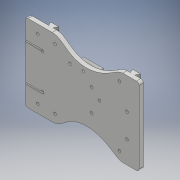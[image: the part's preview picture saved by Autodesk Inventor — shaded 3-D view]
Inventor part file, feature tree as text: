
AUTODESK INVENTOR PART (.ipt)
format: ipt  version: 2017 (Build 210142000, 142)  size: 294,912 bytes
history: native  units: mm
features: sketch x9, extrude x6, hole x3, chamfer x1, fillet x1
ambient origin geometry x8: Origin, YZ Plane, XZ Plane, XY Plane, X Axis, Y Axis, Z Axis, Center Point
bodies: Solid1 (feature_tree)
feature tree (20):
  extrude  "Extrusion1"  Depth=90.0mm
  sketch  "Sketch2"  dims[d2=20.0mm d3=41.0mm]
  extrude  "Extrusion7"  Depth=41.0mm
  extrude  "Extrusion3"  Depth=1.5mm
  extrude  "Extrusion4"  Depth=9.5mm
  extrude  "Extrusion5"  Depth=5.0mm
  hole  "Hole1"  [1 undecoded]
  hole  "Hole2"  [1 undecoded]
  chamfer  "Chamfer1"  Distance=36.0mm
  fillet  "Fillet1"  Radius=11.0mm
  hole  "Hole3"  [1 undecoded]
  extrude  "Extrusion8"  Depth=20.0mm
  sketch  "Sketch1"  dims[d0=132.0mm d1=90.0mm]
  sketch  "Sketch3"  dims[d4=1.5mm d5=1.5mm]
  sketch  "Sketch4"  dims[d6=5.0mm d7=0.0mm d8=9.5mm]
  sketch  "Sketch5"  dims[d10=22.0mm d11=5.0mm]
  sketch  "Sketch6"  dims[d15=4.5mm d23=120.0mm d24=0.0mm]
  sketch  "Sketch7"  dims[d25=3.0mm d26=70.0mm]
  sketch  "Sketch10"  dims[d27=3.0mm]
  sketch  "Sketch11"  dims[d28=20.0mm d29=36.0mm d30=11.0mm d31=0.0mm d32=2.0mm d33=0.0mm d34=20.0mm d35=16.0mm d41=5.0mm d42=5.0mm d45=3.0mm d46=6.0mm d47=4.0mm d48=2.0mm d49=90.0deg d50=8.0mm d51=20.594885mm d52=53.3mm d53=100.0mm d54=20.0mm d55=66.1mm d56=7.6mm d57=33.9mm d58=27.9mm d61=3.0mm d62=6.0mm d63=4.0mm d64=2.0mm d65=90.0deg d66=8.0mm d67=20.594885mm d68=0.5mm d69=2.0mm d70=45.0deg d71=3.0mm d81=50.8mm d82=2.6mm d83=15.3mm d84=4.0mm d86=43.145349mm d88=43.145349mm d90=60.0mm d91=10.0mm d92=0.0mm d93=45.0mm d94=22.5mm d95=22.5mm d100=10.0mm d101=10.0mm d102=10.0mm d103=10.0mm d104=10.0mm d105=10.0mm d106=10.0mm d107=10.0mm d108=3.0mm d109=6.0mm d110=4.0mm d111=2.0mm d112=90.0deg d113=8.0mm d114=20.594885mm d115=10.0mm d116=0.0mm d117=9.0mm d118=15.2mm]
note: 3 required parameter values undecoded (feature->parameter linkage not recoverable at this tier; creation-order binding heuristic only, values carry confidence <= 0.55)
